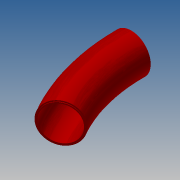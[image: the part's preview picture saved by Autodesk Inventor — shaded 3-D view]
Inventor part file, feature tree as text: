
AUTODESK INVENTOR PART (.ipt)
format: ipt  version: 2017.3 (Build 213257000, 257)  size: 233,984 bytes
history: native  units: in
note: dims shown in document units (in); Inventor stores cm internally (conversion verified against a paired STEP export)
features: revolve x3, extrude x3, sketch x2, plane x1, fillet x1, chamfer x1
ambient origin geometry x8: Origin, YZ Plane, XZ Plane, XY Plane, X Axis, Y Axis, Z Axis, Center Point
bodies: Solid1 (feature_tree)
feature tree (11):
  sketch  "Sketch1"  dims[d0=28.5in d1=32.5in]
  revolve  "Revolution1"  [1 undecoded]
  sketch  "Sketch11"  dims[d2=160.0in d3=30.0deg d37=30.48in d38=33.5in d39=0.25in d40=0.0in d41=0.25in d42=0.0in d43=0.0034in d44=0.0312in d45=0.0312in d46=0.125in d47=45.0deg d48=0.25in d49=0.0137in d50=30.5in d51=0.5in d52=0.0in]
  extrude  "Extrusion10"  TaperAngle=30.0deg  [1 undecoded]
  extrude  "Extrusion11"  Depth=160.0in
  revolve  "Revolution2"  [1 undecoded]
  plane  "Work Plane3"
  revolve  "Revolution3"  [1 undecoded]
  extrude  "Extrusion12"  Depth=160.0in TaperAngle=0.0deg
  fillet  "Fillet3"  Radius=0.0034in
  chamfer  "Chamfer3"  Distance=0.0312in
note: 4 required parameter values undecoded (feature->parameter linkage not recoverable at this tier; creation-order binding heuristic only, values carry confidence <= 0.55)